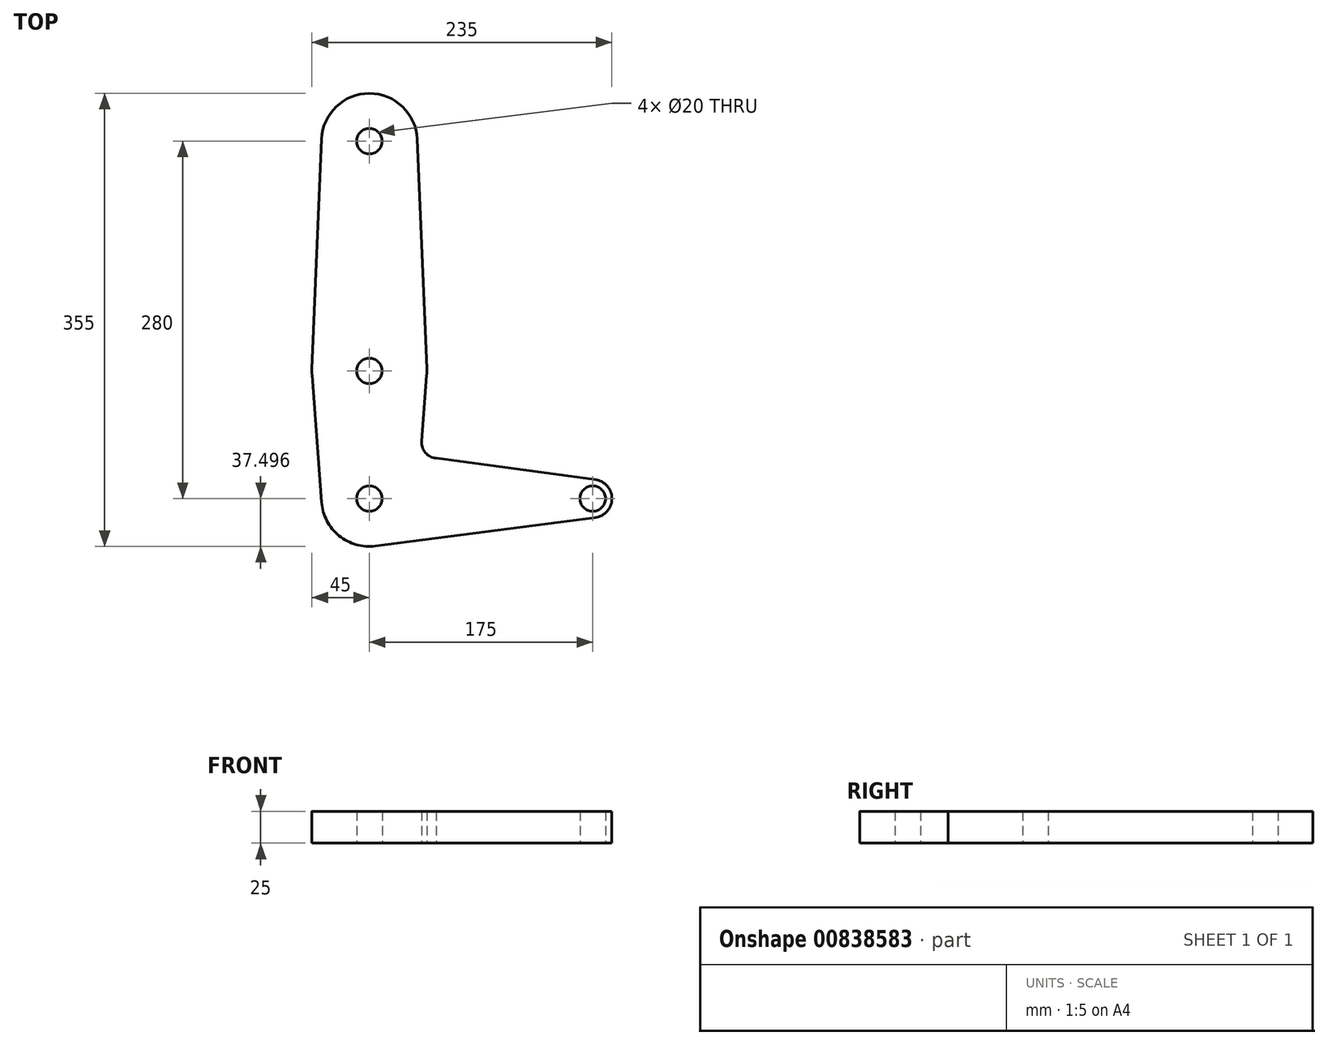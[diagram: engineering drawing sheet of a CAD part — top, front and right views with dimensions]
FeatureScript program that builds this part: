
annotation { "Feature Type Name" : "Feature", "Feature Type Description" : "" }
export const myFeature = defineFeature(function(context is Context, id is Id, definition is map)
    precondition{}
    {
        {
            var Q0;
            Q0=qCreatedBy(makeId("Top.planeOp"),FACE);
            var sketch = newSketch(context, id + "F0", { "sketchPlane" : qUnion([Q0])});
            skLineSegment(sketch, "E0", {"start": v(0, 144.42) * mm, "end": v(0, -135.58) * mm, "construction": true});
            skLineSegment(sketch, "E1", {"start": v(0, -135.58) * mm, "end": v(175, -135.58) * mm, "construction": true});
            skCircle(sketch, "E2", {"center": v(0, 144.42) * mm, "radius": 37.5 * mm});
            skCircle(sketch, "E3", {"center": v(0, -135.58) * mm, "radius": 37.5 * mm});
            skCircle(sketch, "E4", {"center": v(0, -35.58) * mm, "radius": 45 * mm});
            skCircle(sketch, "E5", {"center": v(175, -135.58) * mm, "radius": 15 * mm});
            skLineSegment(sketch, "E6", {"start": v(44.96, -33.7) * mm, "end": v(37.47, 145.98) * mm});
            skLineSegment(sketch, "E7", {"start": v(-44.87, -38.96) * mm, "end": v(-37.4, -138.4) * mm});
            skLineSegment(sketch, "E8", {"start": v(44.87, -38.96) * mm, "end": v(40.98, -90.71) * mm});
            skLineSegment(sketch, "E9", {"start": v(4.82, -172.77) * mm, "end": v(176.93, -150.46) * mm});
            skCircle(sketch, "E10", {"center": v(0, 144.42) * mm, "radius": 10 * mm});
            skCircle(sketch, "E11", {"center": v(0, -35.58) * mm, "radius": 10 * mm});
            skCircle(sketch, "E12", {"center": v(0, -135.58) * mm, "radius": 10 * mm});
            skCircle(sketch, "E13", {"center": v(175, -135.58) * mm, "radius": 10 * mm});
            skArc(sketch, "E14", {"start": v(41, -90.5) * mm, "mid": v(43.94, -99.65) * mm, "end": v(52.52, -104) * mm});
            skLineSegment(sketch, "E15.trimOffspring", {"start": v(37.6, -135.58) * mm, "end": v(37.4, -138.4) * mm});
            skLineSegment(sketch, "E16.trimOffspring", {"start": v(52.3, -103.99) * mm, "end": v(176.93, -120.7) * mm});
            skLineSegment(sketch, "E17", {"start": v(-37.47, 145.98) * mm, "end": v(-44.96, -33.7) * mm});
            skSolve(sketch);
        }
        {
            var Q0;
            Q0=makeQuery(id+"F0.imprint","IMPRINT",FACE,{"disambiguationData":[TD([[makeQuery(id+"F0.imprint","IMPRINT",EDGE,{"derivedFrom":sQuery(id+"F0.wireOp",EDGE,"E10")}),-1.0]])]});
            var Q1;
            {var subQ0=sQuery(id+"F0.wireOp",EDGE,"E6");Q1=makeQuery(id+"F0.imprint","IMPRINT",FACE,{"disambiguationData":[TD([[makeQuery(id+"F0.imprint","IMPRINT",EDGE,{"derivedFrom":subQ0}),1.0]])]});}
            var Q2;
            Q2=makeQuery(id+"F0.imprint","IMPRINT",FACE,{"disambiguationData":[TD([[makeQuery(id+"F0.imprint","IMPRINT",EDGE,{"derivedFrom":sQuery(id+"F0.wireOp",EDGE,"E11")}),-1.0]])]});
            var Q3;
            Q3=makeQuery(id+"F0.imprint","IMPRINT",FACE,{"disambiguationData":[TD([[makeQuery(id+"F0.imprint","IMPRINT",EDGE,{"derivedFrom":sQuery(id+"F0.wireOp",EDGE,"E12")}),-1.0]])]});
            var Q4;
            {var subQ9=sQuery(id+"F0.wireOp",EDGE,"E7");Q4=makeQuery(id+"F0.imprint","IMPRINT",FACE,{"disambiguationData":[TD([[makeQuery(id+"F0.imprint","IMPRINT",EDGE,{"derivedFrom":subQ9}),1.0]])]});}
            var Q5;
            Q5=makeQuery(id+"F0.imprint","IMPRINT",FACE,{"disambiguationData":[TD([[makeQuery(id+"F0.imprint","IMPRINT",EDGE,{"derivedFrom":sQuery(id+"F0.wireOp",EDGE,"E13")}),-1.0]])]});
            extrude(context, id + "F1", {"entities" : qUnion([Q0, Q1, Q2, Q3, Q4, Q5]), "depth" : 25 * mm, "offsetDistance" : 25 * mm});
        }
    });
